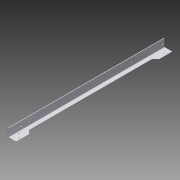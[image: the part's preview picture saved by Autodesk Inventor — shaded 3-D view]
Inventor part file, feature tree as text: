
AUTODESK INVENTOR PART (.ipt)
format: ipt  version: 2015 (Build 190159000, 159)  size: 160,256 bytes
history: native  units: in
note: dims shown in document units (in); Inventor stores cm internally (conversion verified against a paired STEP export)
features: sketch x7, hole x5, extrude x2, projected_geometry x2, fillet x1
ambient origin geometry x8: Origin, YZ Plane, XZ Plane, XY Plane, X Axis, Y Axis, Z Axis, Center Point
bodies: Solid1 (feature_tree)
feature tree (17):
  extrude  "Extrusion1"  Depth=2.0in
  hole  "Hole1"  [1 undecoded]
  hole  "Hole2"  [1 undecoded]
  hole  "Hole3"  [1 undecoded]
  fillet  "Fillet1"  Radius=8.0in
  hole  "Hole5"  [1 undecoded]
  extrude  "Extrusion2"  Depth=1.0in
  hole  "Hole6"  [1 undecoded]
  sketch  "Sketch1"  dims[d0=0.125in d1=2.0in]
  sketch  "Sketch2"  dims[d2=2.0in d3=0.125in]
  sketch  "Sketch3"  dims[d4=38.0in d5=0.0in d6=0.9375in]
  sketch  "Sketch4"  dims[d7=0.9375in d8=0.5in d9=8.0in]
  sketch  "Sketch6"  dims[d10=0.25in d11=0.75in d12=0.375in d13=0.25in d14=0.5635in d15=1.0in d16=0.8108in d17=0.9375in]
  sketch  "Sketch8"  dims[d19=0.375in d20=0.75in d21=0.375in d22=0.25in d23=0.5635in d24=1.0in d25=0.8108in d26=35.0in]
  projected_geometry  "Projected Loop1"
  sketch  "Sketch9"  dims[d27=0.6875in d28=2.0in d29=0.25in d30=0.75in d31=0.375in d32=0.25in d33=0.5635in d34=1.0in d35=0.8108in d36=0.125in d49=1.5in d50=0.5in d51=1.25in d52=0.5in d53=0.1875in d54=0.75in d55=0.375in d56=0.25in d57=0.5635in d58=1.0in d59=0.8108in d60=0.875in d61=4.0in d62=4.0in d63=45.0deg d64=45.0deg d65=1.0in d66=0.0in d67=0.9375in d68=5.0in d69=0.25in d70=0.75in d71=0.375in d72=0.25in d73=0.5635in d74=1.0in d75=0.8108in]
  projected_geometry  "Projected Loop2"
note: 5 required parameter values undecoded (feature->parameter linkage not recoverable at this tier; creation-order binding heuristic only, values carry confidence <= 0.55)
